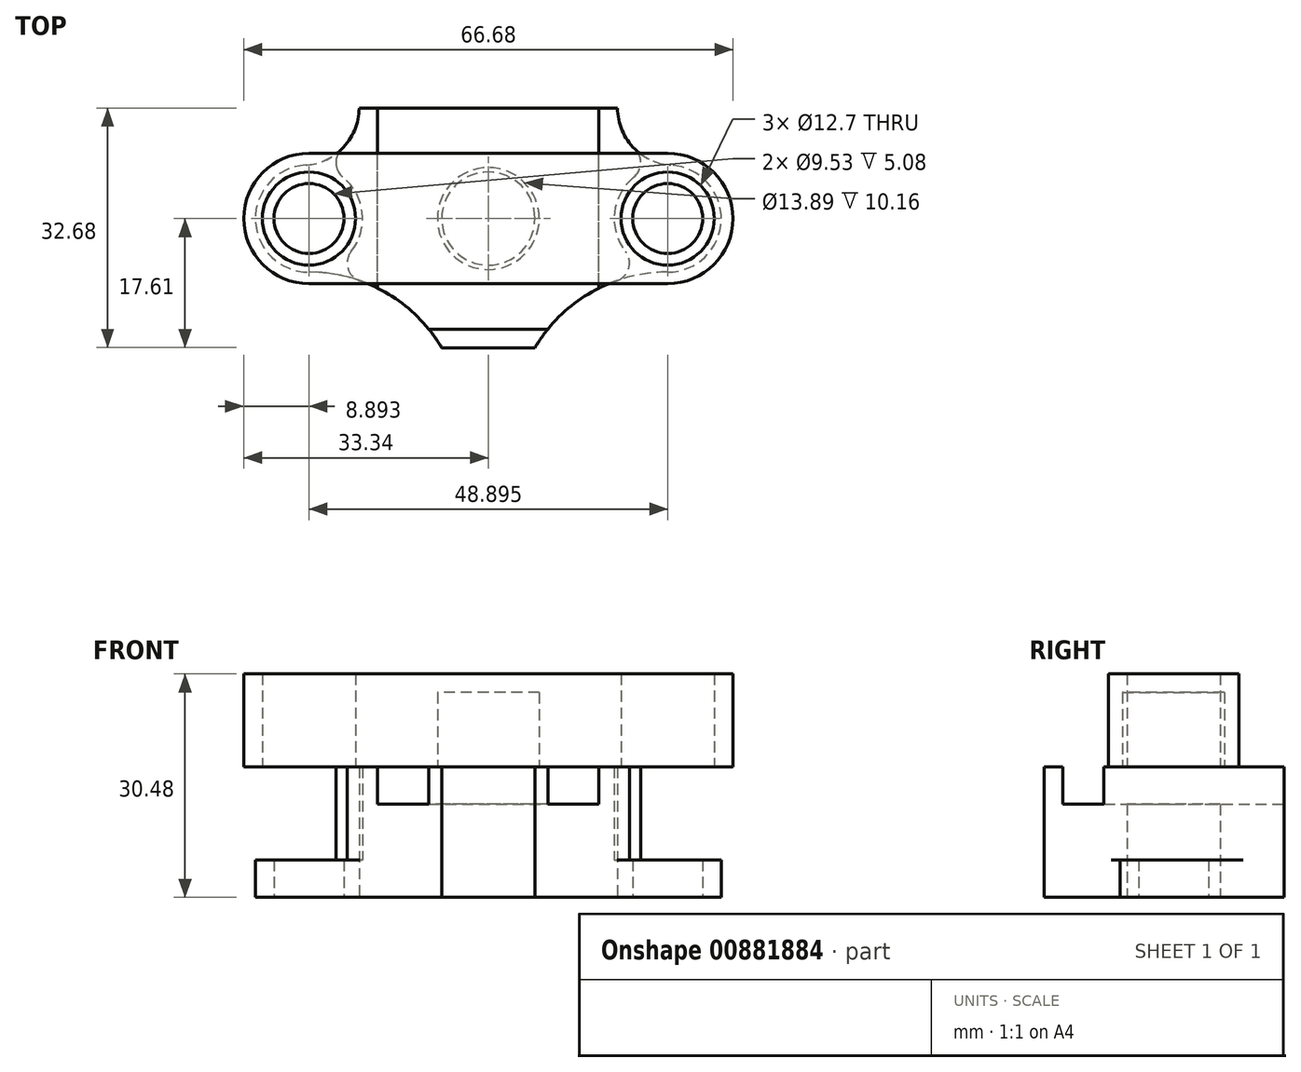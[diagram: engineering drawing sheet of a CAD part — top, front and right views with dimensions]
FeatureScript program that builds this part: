
annotation { "Feature Type Name" : "Feature", "Feature Type Description" : "" }
export const myFeature = defineFeature(function(context is Context, id is Id, definition is map)
    precondition{}
    {
        {
            var Q0;
            Q0=qCreatedBy(makeId("Top.planeOp"),FACE);
            var sketch = newSketch(context, id + "F0", { "sketchPlane" : qUnion([Q0])});
            skLineSegment(sketch, "E0.bottom", {"start": v(15.07, -15.07) * mm, "end": v(-15.07, -15.07) * mm, "construction": true});
            skLineSegment(sketch, "E0.top", {"start": v(15.07, 15.07) * mm, "end": v(-15.07, 15.07) * mm, "construction": true});
            skLineSegment(sketch, "E0.left", {"start": v(15.07, -15.07) * mm, "end": v(15.07, 15.07) * mm, "construction": true});
            skLineSegment(sketch, "E0.right", {"start": v(-15.07, -15.07) * mm, "end": v(-15.07, 15.07) * mm, "construction": true});
            skPoint(sketch, "E0.middle", {"position": v(0, 0) * mm});
            skCircle(sketch, "E1", {"center": v(0, 0) * mm, "radius": 6.35 * mm});
            skCircle(sketch, "E2", {"center": v(-24.45, 0) * mm, "radius": 4.76 * mm});
            skCircle(sketch, "E3", {"center": v(24.45, 0) * mm, "radius": 4.76 * mm});
            skLineSegment(sketch, "E4", {"start": v(-24.45, 0) * mm, "end": v(24.45, 0) * mm, "construction": true});
            skArc(sketch, "E5", {"start": v(-24.92, 7.29) * mm, "mid": v(-31.75, -0.23) * mm, "end": v(-24.45, -7.3) * mm});
            skArc(sketch, "E6", {"start": v(24.45, -7.3) * mm, "mid": v(31.75, -0.23) * mm, "end": v(24.92, 7.29) * mm});
            skLineSegment(sketch, "E7", {"start": v(-6.35, -17.61) * mm, "end": v(6.35, -17.61) * mm});
            skPoint(sketch, "E8", {"position": v(0, -17.61) * mm});
            skArc(sketch, "E9", {"start": v(-6.35, -17.61) * mm, "mid": v(-14.03, -10.06) * mm, "end": v(-24.45, -7.3) * mm});
            skArc(sketch, "E10", {"start": v(24.45, -7.3) * mm, "mid": v(14.03, -10.06) * mm, "end": v(6.35, -17.61) * mm});
            skArc(sketch, "E11", {"start": v(-24.92, 7.29) * mm, "mid": v(-19.73, 9.74) * mm, "end": v(-17.61, 15.07) * mm});
            skArc(sketch, "E12", {"start": v(17.61, 15.07) * mm, "mid": v(19.73, 9.74) * mm, "end": v(24.92, 7.29) * mm});
            skLineSegment(sketch, "E13", {"start": v(-17.61, 15.07) * mm, "end": v(17.61, 15.07) * mm});
            skPoint(sketch, "E14", {"position": v(0, 15.07) * mm});
            skSolve(sketch);
        }
        {
            var Q0;
            Q0 = qSketchRegion(id + "F0", true);
            extrude(context, id + "F1", {"entities" : qUnion([Q0]), "depth" : 5.08 * mm, "offsetDistance" : 25.4 * mm});
        }
        {
            var Q0;
            Q0=makeQuery(id+"F1.opExtrude","CAP_FACE",FACE,{"disambiguationData":[OSD([sQuery(id+"F0.wireOp",EDGE,"E1"),sQuery(id+"F0.wireOp",EDGE,"E2"),sQuery(id+"F0.wireOp",EDGE,"E3"),sQuery(id+"F0.wireOp",EDGE,"E5"),sQuery(id+"F0.wireOp",EDGE,"E6"),sQuery(id+"F0.wireOp",EDGE,"E7"),sQuery(id+"F0.wireOp",EDGE,"E9"),sQuery(id+"F0.wireOp",EDGE,"E10"),sQuery(id+"F0.wireOp",EDGE,"E11"),sQuery(id+"F0.wireOp",EDGE,"E12"),sQuery(id+"F0.wireOp",EDGE,"E13")])],"isStart":false});
            var sketch = newSketch(context, id + "F2", { "sketchPlane" : qUnion([Q0])});
            skArc(sketch, "E15.0", {"start": v(17.54, -8.47) * mm, "mid": v(11.13, -12.05) * mm, "end": v(6.35, -17.61) * mm});
            skArc(sketch, "E16.0", {"start": v(-6.35, -17.61) * mm, "mid": v(-11.13, -12.05) * mm, "end": v(-17.54, -8.47) * mm});
            skLineSegment(sketch, "E17.0", {"start": v(-6.35, -17.61) * mm, "end": v(6.35, -17.61) * mm});
            skCircle(sketch, "E18.0", {"center": v(0, 0) * mm, "radius": 6.35 * mm});
            skLineSegment(sketch, "E19.0", {"start": v(-17.61, 15.07) * mm, "end": v(17.61, 15.07) * mm});
            skArc(sketch, "E20.0", {"start": v(-20, 9.46) * mm, "mid": v(-18.24, 12.03) * mm, "end": v(-17.61, 15.07) * mm});
            skArc(sketch, "E21.0", {"start": v(17.61, 15.07) * mm, "mid": v(18.24, 12.03) * mm, "end": v(20, 9.46) * mm});
            skArc(sketch, "E22", {"start": v(19.84, 5.66) * mm, "mid": v(17.2, 0.81) * mm, "end": v(18.7, -4.5) * mm});
            skArc(sketch, "E23", {"start": v(-18.7, -4.5) * mm, "mid": v(-17.2, 0.81) * mm, "end": v(-19.84, 5.66) * mm});
            skPoint(sketch, "E24.orphan", {"position": v(15.07, 15.07) * mm});
            skPoint(sketch, "E25.orphan", {"position": v(-15.07, 15.07) * mm});
            skPoint(sketch, "E26.0.start.orphan", {"position": v(15.07, -15.07) * mm});
            skPoint(sketch, "E27.0.start.orphan", {"position": v(-15.07, -15.07) * mm});
            skPoint(sketch, "E28.visualSharp", {"position": v(-24.92, 7.29) * mm});
            skArc(sketch, "E28.filletArc", {"start": v(-20, 9.46) * mm, "mid": v(-20.77, 7.53) * mm, "end": v(-19.84, 5.66) * mm});
            skPoint(sketch, "E29.visualSharp", {"position": v(-24.45, -7.3) * mm});
            skArc(sketch, "E29.filletArc", {"start": v(-18.7, -4.5) * mm, "mid": v(-19.14, -6.79) * mm, "end": v(-17.54, -8.47) * mm});
            skPoint(sketch, "E30.visualSharp", {"position": v(24.45, -7.3) * mm});
            skArc(sketch, "E30.filletArc", {"start": v(17.54, -8.47) * mm, "mid": v(19.14, -6.79) * mm, "end": v(18.7, -4.5) * mm});
            skPoint(sketch, "E31.visualSharp", {"position": v(24.92, 7.29) * mm});
            skArc(sketch, "E31.filletArc", {"start": v(19.84, 5.66) * mm, "mid": v(20.77, 7.53) * mm, "end": v(20, 9.46) * mm});
            skSolve(sketch);
        }
        {
            var Q0;
            Q0 = qSketchRegion(id + "F2", true);
            extrude(context, id + "F3", {"entities" : qUnion([Q0]), "operationType" : NewBodyOperationType.ADD, "depth" : 7.62 * mm, "offsetDistance" : 25.4 * mm});
        }
        {
            var Q0;
            Q0=makeQuery(id+"F3.opExtrude","CAP_FACE",FACE,{"disambiguationData":[OSD([sQuery(id+"F2.wireOp",EDGE,"E15.0"),sQuery(id+"F2.wireOp",EDGE,"E16.0"),sQuery(id+"F2.wireOp",EDGE,"E17.0"),sQuery(id+"F2.wireOp",EDGE,"E18.0"),sQuery(id+"F2.wireOp",EDGE,"E19.0"),sQuery(id+"F2.wireOp",EDGE,"E20.0"),sQuery(id+"F2.wireOp",EDGE,"E21.0"),sQuery(id+"F2.wireOp",EDGE,"E22"),sQuery(id+"F2.wireOp",EDGE,"E23"),sQuery(id+"F2.wireOp",EDGE,"E28.filletArc"),sQuery(id+"F2.wireOp",EDGE,"E29.filletArc"),sQuery(id+"F2.wireOp",EDGE,"E30.filletArc"),sQuery(id+"F2.wireOp",EDGE,"E31.filletArc")])],"isStart":false});
            var sketch = newSketch(context, id + "F4", { "sketchPlane" : qUnion([Q0])});
            skLineSegment(sketch, "E32.0", {"start": v(15.07, -9.5) * mm, "end": v(15.07, 15.07) * mm});
            skArc(sketch, "E33.0", {"start": v(19.84, 5.66) * mm, "mid": v(17.2, 0.81) * mm, "end": v(18.7, -4.5) * mm});
            skArc(sketch, "E34.0", {"start": v(17.54, -8.47) * mm, "mid": v(19.14, -6.79) * mm, "end": v(18.7, -4.5) * mm});
            skArc(sketch, "E35.0", {"start": v(17.54, -8.47) * mm, "mid": v(16.29, -8.95) * mm, "end": v(15.07, -9.5) * mm});
            skArc(sketch, "E36.0", {"start": v(17.61, 15.07) * mm, "mid": v(18.24, 12.03) * mm, "end": v(20, 9.46) * mm});
            skLineSegment(sketch, "E37.0", {"start": v(-17.61, 15.07) * mm, "end": v(-15.07, 15.07) * mm});
            skArc(sketch, "E38.0", {"start": v(19.84, 5.66) * mm, "mid": v(20.77, 7.53) * mm, "end": v(20, 9.46) * mm});
            skLineSegment(sketch, "E39.0", {"start": v(-15.07, -9.5) * mm, "end": v(-15.07, 15.07) * mm});
            skLineSegment(sketch, "E40.0", {"start": v(8.12, -15.07) * mm, "end": v(-8.12, -15.07) * mm});
            skLineSegment(sketch, "E41.0", {"start": v(-6.35, -17.61) * mm, "end": v(6.35, -17.61) * mm});
            skArc(sketch, "E42.0", {"start": v(-6.35, -17.61) * mm, "mid": v(-7.19, -16.31) * mm, "end": v(-8.12, -15.07) * mm});
            skArc(sketch, "E43.0", {"start": v(-18.7, -4.5) * mm, "mid": v(-19.14, -6.79) * mm, "end": v(-17.54, -8.47) * mm});
            skArc(sketch, "E44.0", {"start": v(-18.7, -4.5) * mm, "mid": v(-17.2, 0.81) * mm, "end": v(-19.84, 5.66) * mm});
            skArc(sketch, "E45.0", {"start": v(-20, 9.46) * mm, "mid": v(-18.24, 12.03) * mm, "end": v(-17.61, 15.07) * mm});
            skArc(sketch, "E46.0", {"start": v(-20, 9.46) * mm, "mid": v(-20.77, 7.53) * mm, "end": v(-19.84, 5.66) * mm});
            skPoint(sketch, "E47.orphan", {"position": v(15.07, -15.07) * mm});
            skPoint(sketch, "E48.orphan", {"position": v(-15.07, -15.07) * mm});
            skArc(sketch, "E49.trimOffspring", {"start": v(8.12, -15.07) * mm, "mid": v(7.19, -16.31) * mm, "end": v(6.35, -17.61) * mm});
            skArc(sketch, "E50.trimOffspring", {"start": v(-15.07, -9.5) * mm, "mid": v(-16.29, -8.95) * mm, "end": v(-17.54, -8.47) * mm});
            skLineSegment(sketch, "E51.trimOffspring", {"start": v(15.07, 15.07) * mm, "end": v(17.61, 15.07) * mm});
            skPoint(sketch, "E52.orphan", {"position": v(24.92, 7.29) * mm});
            skPoint(sketch, "E53.orphan", {"position": v(24.45, -7.3) * mm});
            skPoint(sketch, "E54.orphan", {"position": v(-24.45, -7.3) * mm});
            skPoint(sketch, "E55.orphan", {"position": v(-24.92, 7.29) * mm});
            skSolve(sketch);
        }
        {
            var Q0;
            Q0 = qSketchRegion(id + "F4", true);
            extrude(context, id + "F5", {"entities" : qUnion([Q0]), "operationType" : NewBodyOperationType.ADD, "depth" : 5.08 * mm, "offsetDistance" : 25.4 * mm});
        }
        {
            var Q0;
            Q0=makeQuery(id+"F5.opExtrude","CAP_FACE",FACE,{"disambiguationData":[OSD([sQuery(id+"F4.wireOp",EDGE,"E32.0"),sQuery(id+"F4.wireOp",EDGE,"E33.0"),sQuery(id+"F4.wireOp",EDGE,"E34.0"),sQuery(id+"F4.wireOp",EDGE,"E35.0"),sQuery(id+"F4.wireOp",EDGE,"E36.0"),sQuery(id+"F4.wireOp",EDGE,"E38.0"),sQuery(id+"F4.wireOp",EDGE,"E51.trimOffspring")])],"isStart":false});
            var sketch = newSketch(context, id + "F6", { "sketchPlane" : qUnion([Q0])});
            skCircle(sketch, "E56", {"center": v(24.45, 0) * mm, "radius": 6.35 * mm});
            skCircle(sketch, "E57", {"center": v(-24.45, 0) * mm, "radius": 6.35 * mm});
            skArc(sketch, "E58", {"start": v(24.45, -8.89) * mm, "mid": v(33.34, 0) * mm, "end": v(24.45, 8.9) * mm});
            skArc(sketch, "E59", {"start": v(-24.45, 8.9) * mm, "mid": v(-33.34, 0) * mm, "end": v(-24.45, -8.89) * mm});
            skCircle(sketch, "E60", {"center": v(0, 0) * mm, "radius": 6.95 * mm});
            skLineSegment(sketch, "E61", {"start": v(-24.45, 8.9) * mm, "end": v(24.45, 8.9) * mm});
            skLineSegment(sketch, "E62", {"start": v(24.45, -8.89) * mm, "end": v(-24.45, -8.89) * mm});
            skSolve(sketch);
        }
        {
            var Q0;
            Q0 = qSketchRegion(id + "F6", true);
            extrude(context, id + "F7", {"entities" : qUnion([Q0]), "depth" : 12.7 * mm, "offsetDistance" : 25.4 * mm});
        }
        {
            var Q0;
            Q0=makeQuery(id+"F7.opExtrude","CAP_FACE",FACE,{"disambiguationData":[OSD([sQuery(id+"F6.wireOp",EDGE,"E56"),sQuery(id+"F6.wireOp",EDGE,"E57"),sQuery(id+"F6.wireOp",EDGE,"E58"),sQuery(id+"F6.wireOp",EDGE,"E59"),sQuery(id+"F6.wireOp",EDGE,"E60"),sQuery(id+"F6.wireOp",EDGE,"E61"),sQuery(id+"F6.wireOp",EDGE,"E62")])],"isStart":false});
            var sketch = newSketch(context, id + "F8", { "sketchPlane" : qUnion([Q0])});
            skCircle(sketch, "E63.0", {"center": v(0, 0) * mm, "radius": 6.95 * mm});
            skSolve(sketch);
        }
        {
            var Q0;
            Q0 = qSketchRegion(id + "F8", true);
            extrude(context, id + "F9", {"entities" : qUnion([Q0]), "operationType" : NewBodyOperationType.ADD, "oppositeDirection" : true, "depth" : 2.54 * mm, "offsetDistance" : 25.4 * mm});
        }
    });
